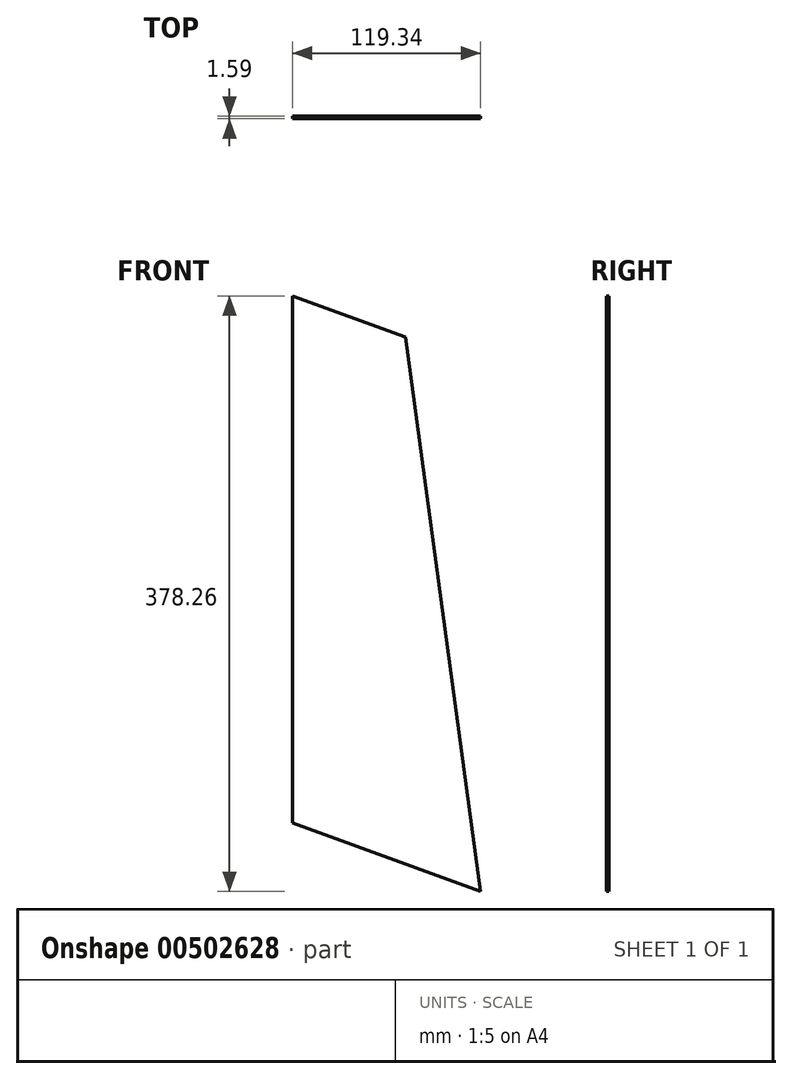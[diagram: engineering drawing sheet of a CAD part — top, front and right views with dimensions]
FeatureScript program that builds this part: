
annotation { "Feature Type Name" : "Feature", "Feature Type Description" : "" }
export const myFeature = defineFeature(function(context is Context, id is Id, definition is map)
    precondition{}
    {
        {
            var Q0;
            Q0=qCreatedBy(makeId("Front.planeOp"),FACE);
            var sketch = newSketch(context, id + "F0", { "sketchPlane" : qUnion([Q0])});
            skLineSegment(sketch, "E0", {"start": v(0, 0) * mm, "end": v(0, 334.82) * mm});
            skLineSegment(sketch, "E1", {"start": v(0, 334.82) * mm, "end": v(71.6, 308.76) * mm});
            skLineSegment(sketch, "E2", {"start": v(71.6, 308.76) * mm, "end": v(119.34, -43.44) * mm});
            skLineSegment(sketch, "E3", {"start": v(119.34, -43.44) * mm, "end": v(0, 0) * mm});
            skSolve(sketch);
        }
        {
            var Q0;
            Q0=makeQuery(id+"F0.imprint","IMPRINT",FACE,{"disambiguationData":[TD([[makeQuery(id+"F0.imprint","IMPRINT",EDGE,{"derivedFrom":sQuery(id+"F0.wireOp",EDGE,"E0")}),-1.0]])]});
            extrude(context, id + "F1", {"entities" : qUnion([Q0]), "depth" : 1.59 * mm});
        }
    });
